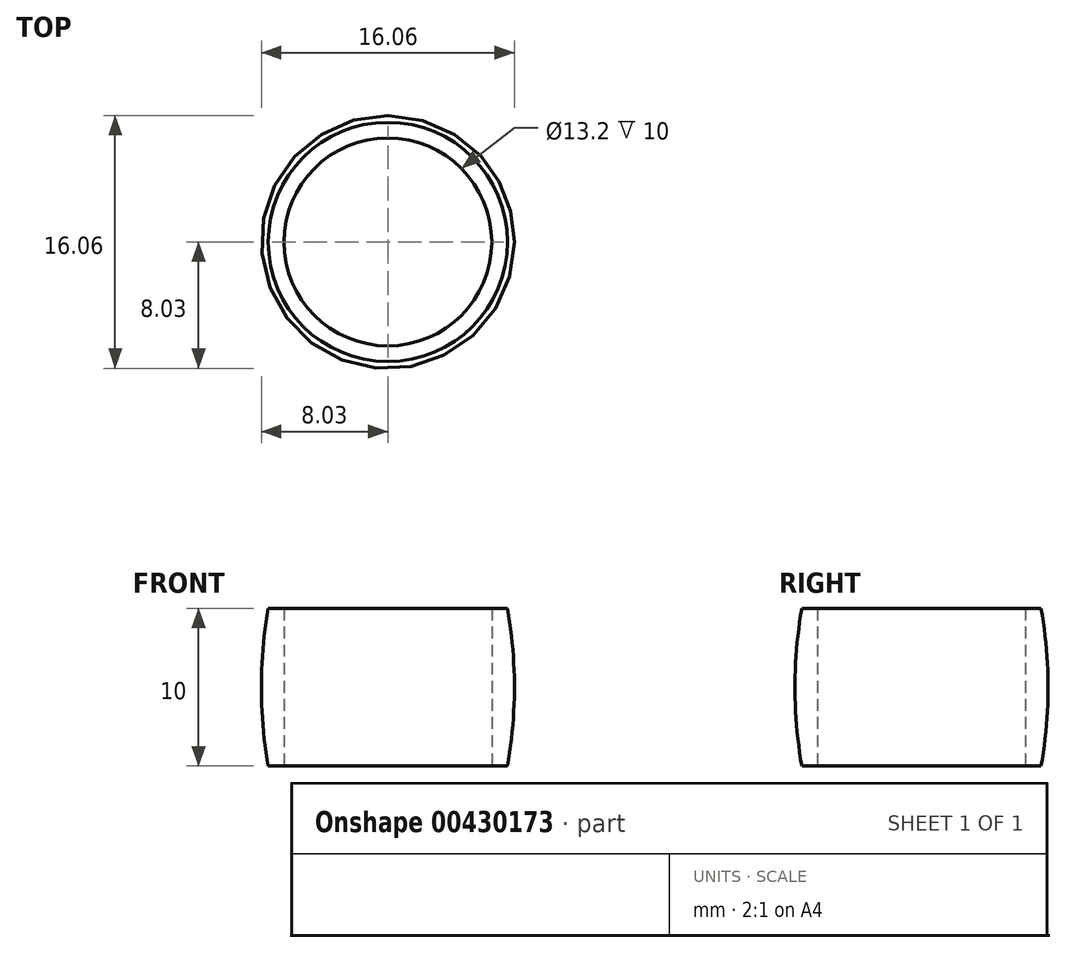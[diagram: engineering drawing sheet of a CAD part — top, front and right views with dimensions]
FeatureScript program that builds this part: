
annotation { "Feature Type Name" : "Feature", "Feature Type Description" : "" }
export const myFeature = defineFeature(function(context is Context, id is Id, definition is map)
    precondition{}
    {
        {
            var Q0;
            Q0=qCreatedBy(makeId("Top.planeOp"),FACE);
            var sketch = newSketch(context, id + "F0", { "sketchPlane" : qUnion([Q0])});
            skCircle(sketch, "E0", {"center": v(0, 0) * mm, "radius": 6.6 * mm});
            skCircle(sketch, "E1", {"center": v(0, 0) * mm, "radius": 7.6 * mm});
            skSolve(sketch);
        }
        {
            var Q0;
            Q0 = qSketchRegion(id + "F0", true);
            extrude(context, id + "F1", {"entities" : qUnion([Q0]), "depth" : 10 * mm});
        }
        {
            var Q0;
            Q0=qCreatedBy(makeId("Right.planeOp"),FACE);
            var sketch = newSketch(context, id + "F2", { "sketchPlane" : qUnion([Q0])});
            skLineSegment(sketch, "E2.0", {"start": v(-7.6, 10) * mm, "end": v(7.6, 10) * mm});
            skLineSegment(sketch, "E3.0", {"start": v(-7.6, 0) * mm, "end": v(7.6, 0) * mm});
            skArc(sketch, "E4", {"start": v(7.6, 0) * mm, "mid": v(8.03, 5) * mm, "end": v(7.6, 10) * mm});
            skLineSegment(sketch, "E5", {"start": v(7.6, 10) * mm, "end": v(7.6, 0) * mm});
            skSolve(sketch);
        }
        {
            var Q0;
            Q0=makeQuery(id+"F2.imprint","IMPRINT",FACE,{"disambiguationData":[TD([[makeQuery(id+"F2.imprint","IMPRINT",EDGE,{"derivedFrom":sQuery(id+"F2.wireOp",EDGE,"E4")}),1.0]])]});
            var Q1;
            Q1=makeQuery(id+"F1.opExtrude","CAP_EDGE",EDGE,{"disambiguationData":[OSD([sQuery(id+"F0.wireOp",EDGE,"E0")])],"isStart":false});
            revolve(context, id + "F3", {"operationType" : NewBodyOperationType.ADD, "entities" : qUnion([Q0]), "axis" : qUnion([Q1]), "revolveType" : RevolveType.FULL});
        }
    });
